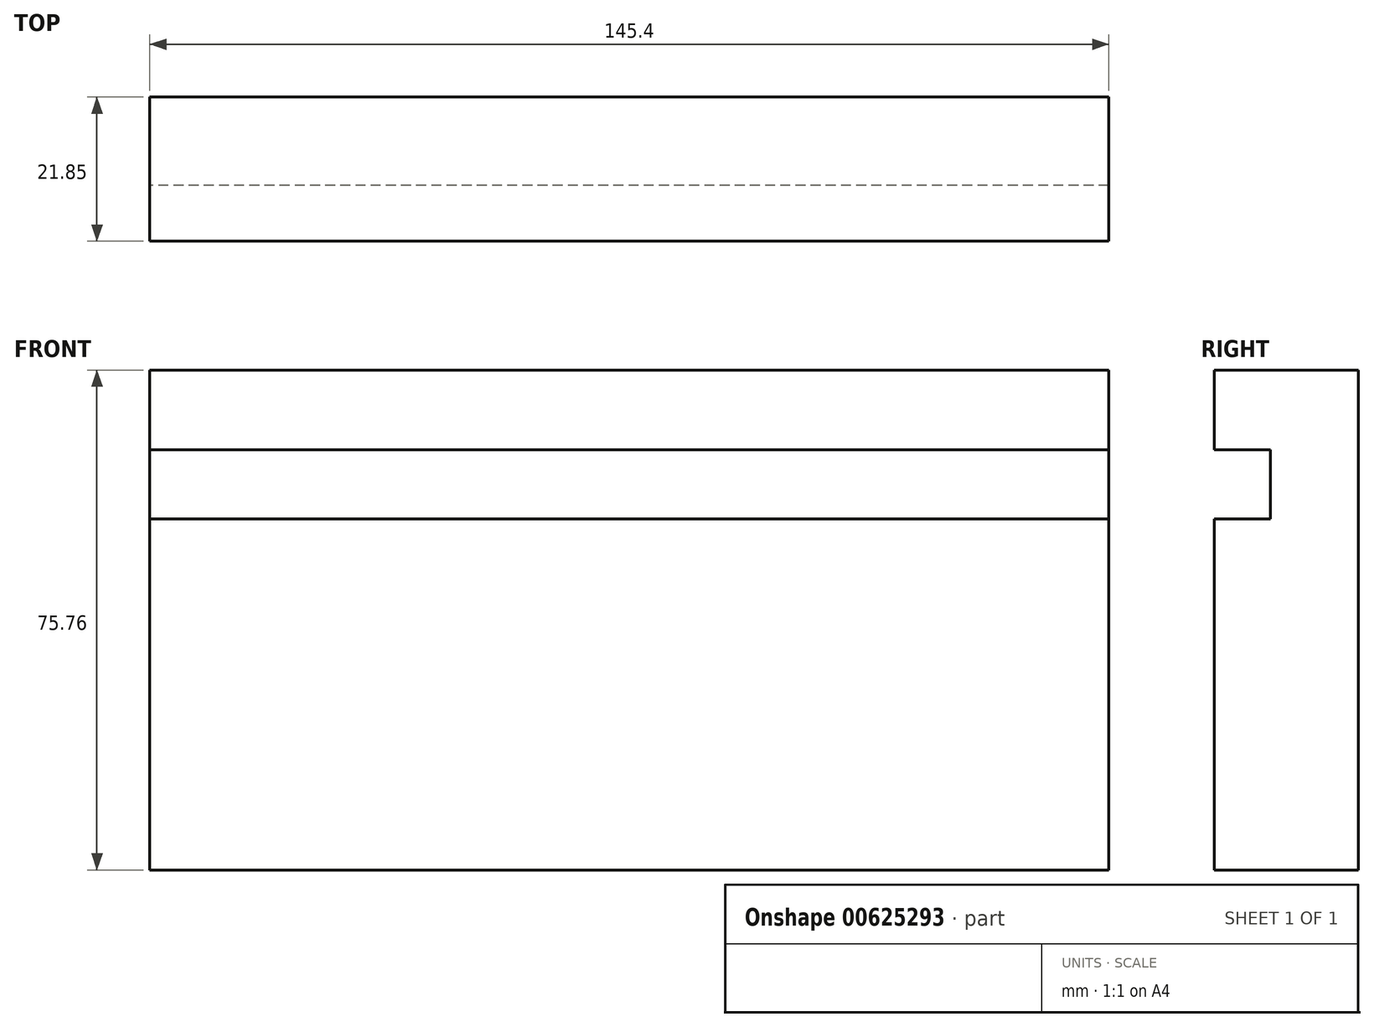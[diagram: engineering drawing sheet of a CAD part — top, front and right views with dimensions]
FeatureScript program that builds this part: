
annotation { "Feature Type Name" : "Feature", "Feature Type Description" : "" }
export const myFeature = defineFeature(function(context is Context, id is Id, definition is map)
    precondition{}
    {
        {
            var Q0;
            Q0=qCreatedBy(makeId("Right.planeOp"),FACE);
            var sketch = newSketch(context, id + "F0", { "sketchPlane" : qUnion([Q0])});
            skLineSegment(sketch, "E0", {"start": v(0, 0) * mm, "end": v(0, 75.76) * mm});
            skLineSegment(sketch, "E1", {"start": v(0, 75.76) * mm, "end": v(-21.85, 75.76) * mm});
            skLineSegment(sketch, "E2", {"start": v(-21.85, 63.7) * mm, "end": v(-13.37, 63.7) * mm});
            skLineSegment(sketch, "E3", {"start": v(-13.37, 63.7) * mm, "end": v(-13.37, 53.19) * mm});
            skLineSegment(sketch, "E4", {"start": v(-13.37, 53.19) * mm, "end": v(-21.85, 53.19) * mm});
            skLineSegment(sketch, "E5", {"start": v(-21.85, 53.19) * mm, "end": v(-21.85, 0) * mm});
            skLineSegment(sketch, "E6", {"start": v(-21.85, 0) * mm, "end": v(0, 0) * mm});
            skLineSegment(sketch, "E7", {"start": v(-21.85, 63.7) * mm, "end": v(-21.85, 75.76) * mm});
            skSolve(sketch);
        }
        {
            var Q0;
            Q0 = qSketchRegion(id + "F0", true);
            extrude(context, id + "F1", {"entities" : qUnion([Q0]), "depth" : 120 * mm, "offsetDistance" : 25.4 * mm, "hasSecondDirection" : true, "secondDirectionOppositeDirection" : true, "secondDirectionDepth" : 25.4 * mm});
        }
    });
